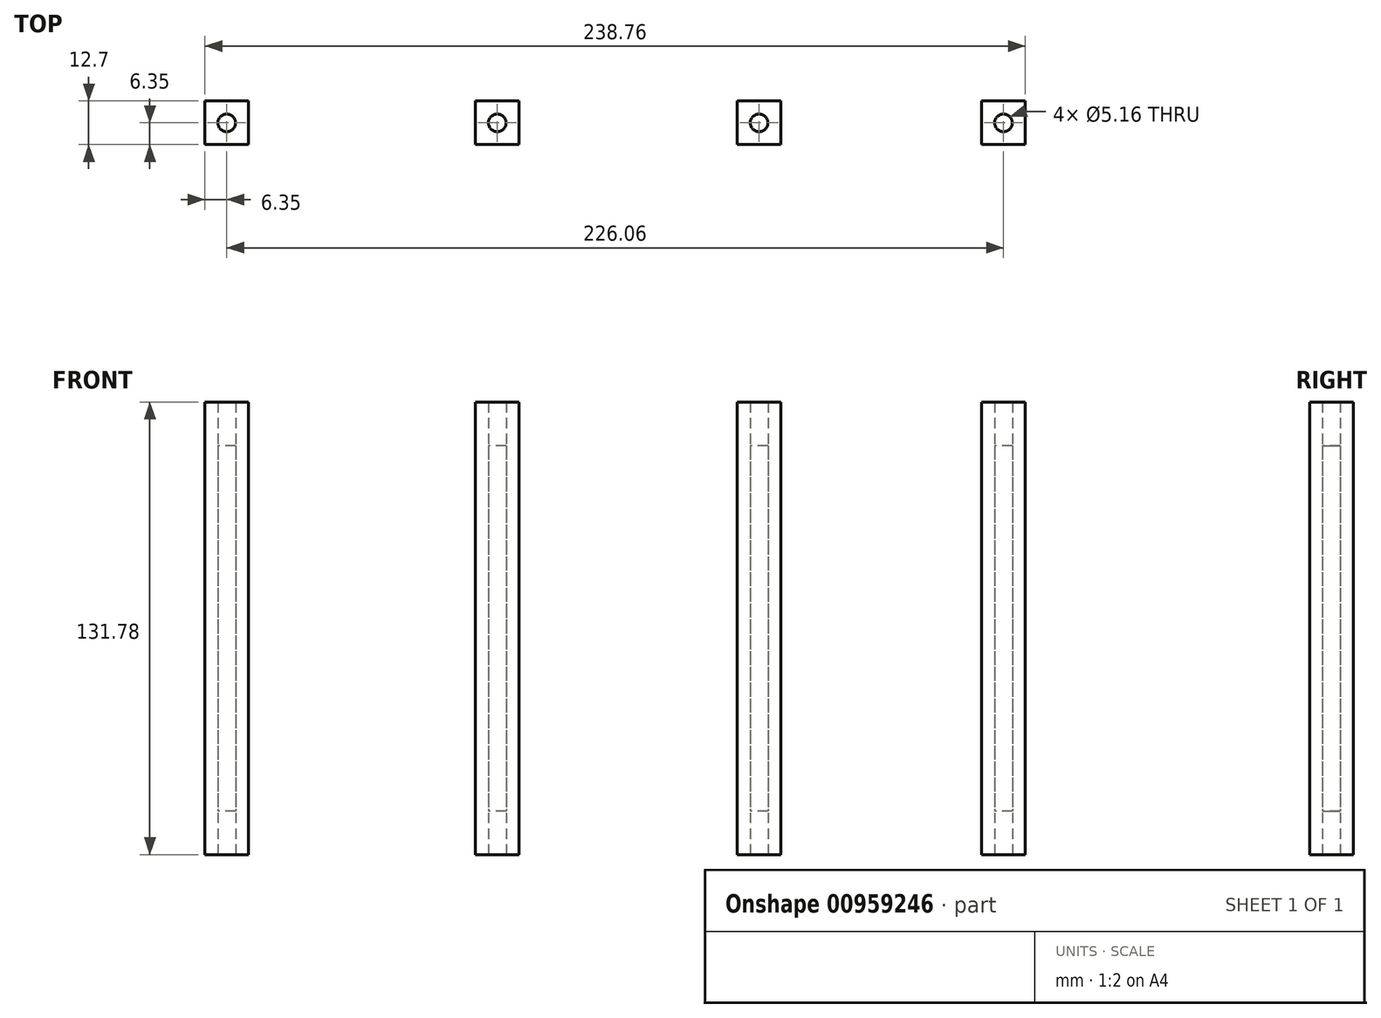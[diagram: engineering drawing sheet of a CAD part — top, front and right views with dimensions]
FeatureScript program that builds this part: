
annotation { "Feature Type Name" : "Feature", "Feature Type Description" : "" }
export const myFeature = defineFeature(function(context is Context, id is Id, definition is map)
    precondition{}
    {
        {
            var Q0;
            Q0=qCreatedBy(makeId("Top.planeOp"),FACE);
            var sketch = newSketch(context, id + "F0", { "sketchPlane" : qUnion([Q0])});
            skLineSegment(sketch, "E0.bottom", {"start": v(-78.74, 12.7) * mm, "end": v(-66.04, 12.7) * mm});
            skLineSegment(sketch, "E0.top", {"start": v(-78.74, 0) * mm, "end": v(-66.04, 0) * mm});
            skLineSegment(sketch, "E0.left", {"start": v(-78.74, 12.7) * mm, "end": v(-78.74, 0) * mm});
            skLineSegment(sketch, "E0.right", {"start": v(-66.04, 12.7) * mm, "end": v(-66.04, 0) * mm});
            skLineSegment(sketch, "E1.bottom", {"start": v(147.32, 12.7) * mm, "end": v(160.02, 12.7) * mm});
            skLineSegment(sketch, "E1.top", {"start": v(147.32, 0) * mm, "end": v(160.02, 0) * mm});
            skLineSegment(sketch, "E1.left", {"start": v(147.32, 12.7) * mm, "end": v(147.32, 0) * mm});
            skLineSegment(sketch, "E1.right", {"start": v(160.02, 12.7) * mm, "end": v(160.02, 0) * mm});
            skLineSegment(sketch, "E2.bottom", {"start": v(76.2, 12.7) * mm, "end": v(88.9, 12.7) * mm});
            skLineSegment(sketch, "E2.top", {"start": v(76.2, 0) * mm, "end": v(88.9, 0) * mm});
            skLineSegment(sketch, "E2.left", {"start": v(76.2, 12.7) * mm, "end": v(76.2, 0) * mm});
            skLineSegment(sketch, "E2.right", {"start": v(88.9, 12.7) * mm, "end": v(88.9, 0) * mm});
            skLineSegment(sketch, "E3.bottom", {"start": v(0, 12.7) * mm, "end": v(12.7, 12.7) * mm});
            skLineSegment(sketch, "E3.top", {"start": v(0, 0) * mm, "end": v(12.7, 0) * mm});
            skLineSegment(sketch, "E3.left", {"start": v(0, 12.7) * mm, "end": v(0, 0) * mm});
            skLineSegment(sketch, "E3.right", {"start": v(12.7, 12.7) * mm, "end": v(12.7, 0) * mm});
            skCircle(sketch, "E4", {"center": v(6.35, 6.35) * mm, "radius": 2.58 * mm});
            skCircle(sketch, "E5", {"center": v(82.55, 6.35) * mm, "radius": 2.58 * mm});
            skCircle(sketch, "E6", {"center": v(153.67, 6.35) * mm, "radius": 2.58 * mm});
            skCircle(sketch, "E7", {"center": v(-72.4, 6.35) * mm, "radius": 2.58 * mm});
            skSolve(sketch);
        }
        {
            var Q0;
            Q0=makeQuery(id+"F0.imprint","IMPRINT",FACE,{"disambiguationData":[TD([[makeQuery(id+"F0.imprint","IMPRINT",EDGE,{"derivedFrom":sQuery(id+"F0.wireOp",EDGE,"E0.bottom")}),-1.0]])]});
            var Q1;
            Q1=makeQuery(id+"F0.imprint","IMPRINT",FACE,{"disambiguationData":[TD([[makeQuery(id+"F0.imprint","IMPRINT",EDGE,{"derivedFrom":sQuery(id+"F0.wireOp",EDGE,"E3.bottom")}),-1.0]])]});
            var Q2;
            Q2=makeQuery(id+"F0.imprint","IMPRINT",FACE,{"disambiguationData":[TD([[makeQuery(id+"F0.imprint","IMPRINT",EDGE,{"derivedFrom":sQuery(id+"F0.wireOp",EDGE,"E2.bottom")}),-1.0]])]});
            var Q3;
            Q3=makeQuery(id+"F0.imprint","IMPRINT",FACE,{"disambiguationData":[TD([[makeQuery(id+"F0.imprint","IMPRINT",EDGE,{"derivedFrom":sQuery(id+"F0.wireOp",EDGE,"E1.bottom")}),-1.0]])]});
            extrude(context, id + "F1", {"entities" : qUnion([Q0, Q1, Q2, Q3]), "depth" : 131.78 * mm, "offsetDistance" : 25.4 * mm});
        }
        {
            var Q0;
            Q0=makeQuery(id+"F0.imprint","IMPRINT",FACE,{"disambiguationData":[TD([[makeQuery(id+"F0.imprint","IMPRINT",EDGE,{"derivedFrom":sQuery(id+"F0.wireOp",EDGE,"E7")}),1.0]])]});
            var Q1;
            Q1=makeQuery(id+"F0.imprint","IMPRINT",FACE,{"disambiguationData":[TD([[makeQuery(id+"F0.imprint","IMPRINT",EDGE,{"derivedFrom":sQuery(id+"F0.wireOp",EDGE,"E4")}),1.0]])]});
            var Q2;
            Q2=makeQuery(id+"F0.imprint","IMPRINT",FACE,{"disambiguationData":[TD([[makeQuery(id+"F0.imprint","IMPRINT",EDGE,{"derivedFrom":sQuery(id+"F0.wireOp",EDGE,"E5")}),1.0]])]});
            var Q3;
            Q3=makeQuery(id+"F0.imprint","IMPRINT",FACE,{"disambiguationData":[TD([[makeQuery(id+"F0.imprint","IMPRINT",EDGE,{"derivedFrom":sQuery(id+"F0.wireOp",EDGE,"E6")}),1.0]])]});
            extrude(context, id + "F2", {"entities" : qUnion([Q0, Q1, Q2, Q3]), "depth" : 106.38 * mm, "offsetDistance" : 25.4 * mm});
        }
        {
            var Q0;
            Q0=makeQuery(id+"F2.opExtrude","SWEPT_BODY",BODY,{"disambiguationData":[OSD([sQuery(id+"F0.wireOp",EDGE,"E6")])]});
            var Q1;
            Q1=makeQuery(id+"F2.opExtrude","SWEPT_BODY",BODY,{"disambiguationData":[OSD([sQuery(id+"F0.wireOp",EDGE,"E5")])]});
            var Q2;
            Q2=makeQuery(id+"F2.opExtrude","SWEPT_BODY",BODY,{"disambiguationData":[OSD([sQuery(id+"F0.wireOp",EDGE,"E4")])]});
            var Q3;
            Q3=makeQuery(id+"F2.opExtrude","SWEPT_BODY",BODY,{"disambiguationData":[OSD([sQuery(id+"F0.wireOp",EDGE,"E7")])]});
            transform(context, id + "F3", {"entities" : qUnion([Q0, Q1, Q2, Q3]), "transformType" : TransformType.TRANSLATION_3D, "dx" : 0 * mm, "dy" : 0 * mm, "dz" : 12.7 * mm, "makeCopy" : false});
        }
    });
